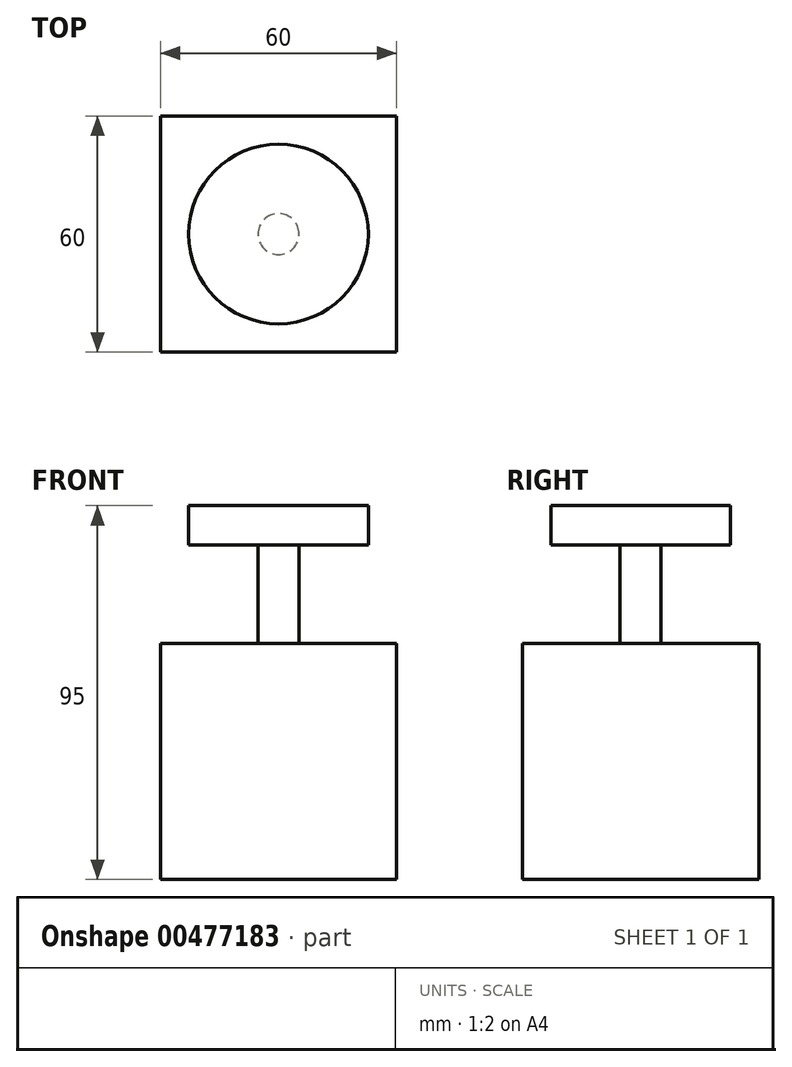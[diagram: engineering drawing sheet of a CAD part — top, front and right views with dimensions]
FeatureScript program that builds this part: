
annotation { "Feature Type Name" : "Feature", "Feature Type Description" : "" }
export const myFeature = defineFeature(function(context is Context, id is Id, definition is map)
    precondition{}
    {
        {
            var Q0;
            Q0=qCreatedBy(makeId("Top.planeOp"),FACE);
            var sketch = newSketch(context, id + "F0", { "sketchPlane" : qUnion([Q0])});
            skLineSegment(sketch, "E0.bottom", {"start": v(30, -30) * mm, "end": v(-30, -30) * mm});
            skLineSegment(sketch, "E0.top", {"start": v(30, 30) * mm, "end": v(-30, 30) * mm});
            skLineSegment(sketch, "E0.left", {"start": v(30, -30) * mm, "end": v(30, 30) * mm});
            skLineSegment(sketch, "E0.right", {"start": v(-30, -30) * mm, "end": v(-30, 30) * mm});
            skPoint(sketch, "E0.middle", {"position": v(0, 0) * mm});
            skSolve(sketch);
        }
        {
            var Q0;
            Q0 = qSketchRegion(id + "F0", true);
            extrude(context, id + "F1", {"entities" : qUnion([Q0]), "depth" : 60 * mm});
        }
        {
            var Q0;
            Q0=makeQuery(id+"F1.opExtrude","CAP_FACE",FACE,{"disambiguationData":[OSD([sQuery(id+"F0.wireOp",EDGE,"E0.bottom"),sQuery(id+"F0.wireOp",EDGE,"E0.top"),sQuery(id+"F0.wireOp",EDGE,"E0.left"),sQuery(id+"F0.wireOp",EDGE,"E0.right")])],"isStart":false});
            var sketch = newSketch(context, id + "F2", { "sketchPlane" : qUnion([Q0])});
            skCircle(sketch, "E1", {"center": v(0, 0) * mm, "radius": 5.2 * mm});
            skSolve(sketch);
        }
        {
            var Q0;
            Q0 = qSketchRegion(id + "F2", true);
            extrude(context, id + "F3", {"entities" : qUnion([Q0]), "operationType" : NewBodyOperationType.ADD, "depth" : 25 * mm});
        }
        {
            var Q0;
            Q0=makeQuery(id+"F3.opExtrude","CAP_FACE",FACE,{"disambiguationData":[OSD([sQuery(id+"F2.wireOp",EDGE,"E1")])],"isStart":false});
            var sketch = newSketch(context, id + "F4", { "sketchPlane" : qUnion([Q0])});
            skCircle(sketch, "E2", {"center": v(0, 0) * mm, "radius": 22.8 * mm});
            skSolve(sketch);
        }
        {
            var Q0;
            Q0 = qSketchRegion(id + "F4", true);
            extrude(context, id + "F5", {"entities" : qUnion([Q0]), "operationType" : NewBodyOperationType.ADD, "depth" : 10 * mm});
        }
    });
